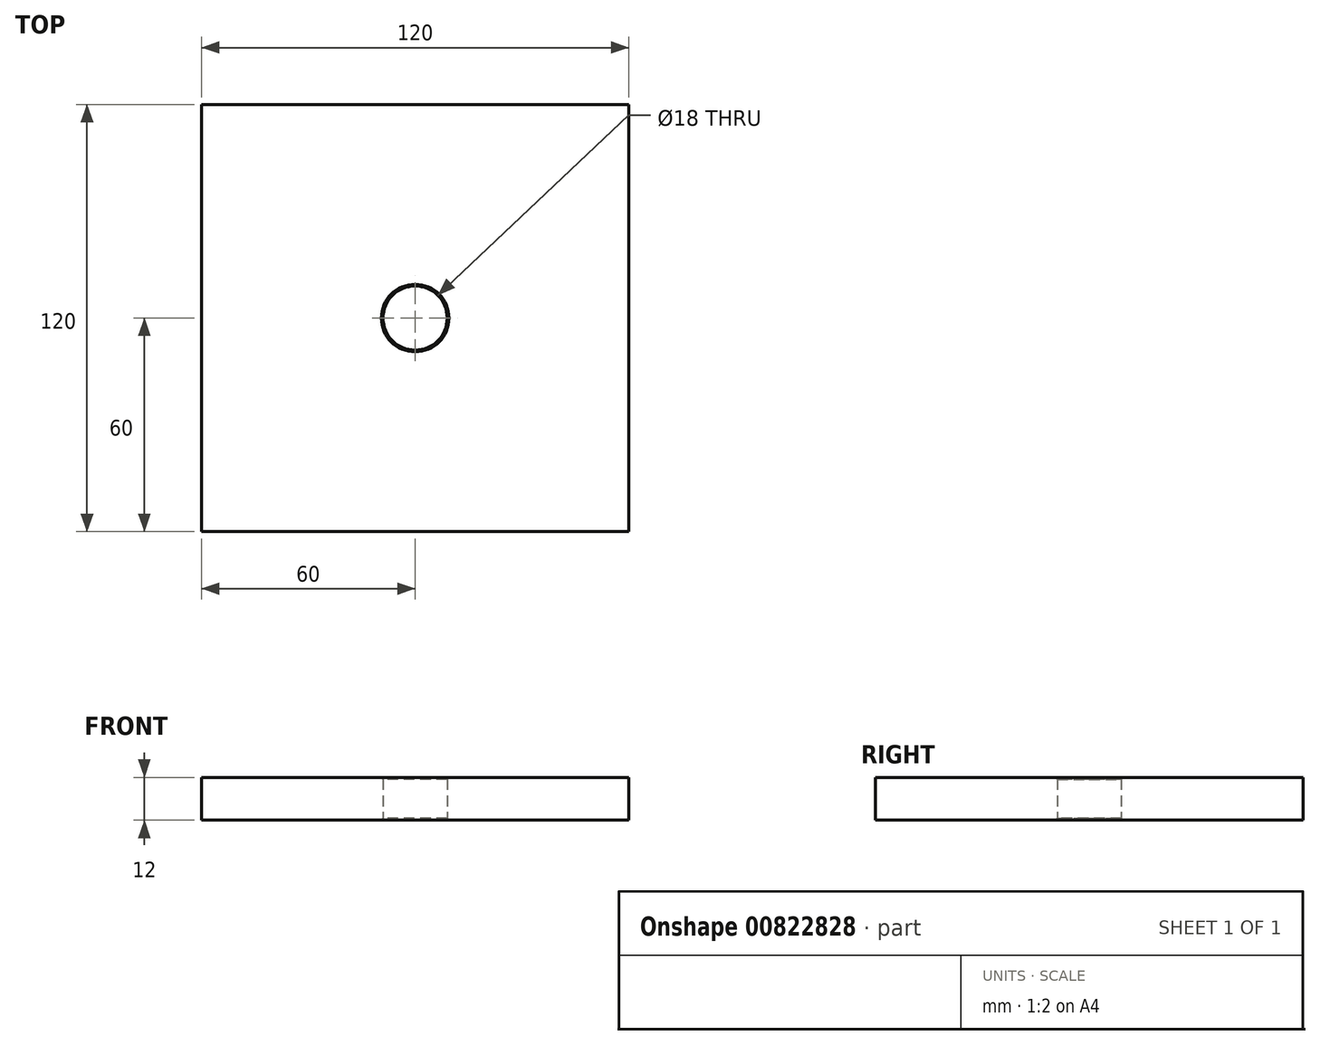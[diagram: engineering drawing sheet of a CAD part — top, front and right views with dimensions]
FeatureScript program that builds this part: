
annotation { "Feature Type Name" : "Feature", "Feature Type Description" : "" }
export const myFeature = defineFeature(function(context is Context, id is Id, definition is map)
    precondition{}
    {
        {
            var Q0;
            Q0=qCreatedBy(makeId("Top.planeOp"),FACE);
            var sketch = newSketch(context, id + "F0", { "sketchPlane" : qUnion([Q0])});
            skLineSegment(sketch, "E0.bottom", {"start": v(-60, -60) * mm, "end": v(60, -60) * mm});
            skLineSegment(sketch, "E0.top", {"start": v(-60, 60) * mm, "end": v(60, 60) * mm});
            skLineSegment(sketch, "E0.left", {"start": v(-60, -60) * mm, "end": v(-60, 60) * mm});
            skLineSegment(sketch, "E0.right", {"start": v(60, -60) * mm, "end": v(60, 60) * mm});
            skPoint(sketch, "E0.middle", {"position": v(0, 0) * mm});
            skLineSegment(sketch, "E1", {"start": v(0, 0) * mm, "end": v(0, 29.5) * mm, "construction": true});
            skLineSegment(sketch, "E2.bottom", {"start": v(-50.7, 9) * mm, "end": v(50.7, 9) * mm, "construction": true});
            skLineSegment(sketch, "E2.top", {"start": v(-50.7, 50) * mm, "end": v(50.7, 50) * mm, "construction": true});
            skLineSegment(sketch, "E2.left", {"start": v(-50.7, 9) * mm, "end": v(-50.7, 50) * mm, "construction": true});
            skLineSegment(sketch, "E2.right", {"start": v(50.7, 9) * mm, "end": v(50.7, 50) * mm, "construction": true});
            skPoint(sketch, "E2.middle", {"position": v(0, 29.5) * mm});
            skLineSegment(sketch, "E3.0", {"start": v(-50.7, 43.7) * mm, "end": v(50.7, 43.7) * mm, "construction": true});
            skCircle(sketch, "E4", {"center": v(0, 0) * mm, "radius": 9 * mm});
            skSolve(sketch);
        }
        {
            var Q0;
            Q0 = qSketchRegion(id + "F0", true);
            extrude(context, id + "F1", {"entities" : qUnion([Q0]), "depth" : 12 * mm, "offsetDistance" : 25 * mm});
        }
        {
            var Q0;
            Q0=makeQuery(id+"F1.opExtrude","SWEPT_FACE",FACE,{"disambiguationData":[OSD([sQuery(id+"F0.wireOp",EDGE,"E4")])]});
            chamfer(context, id + "F2", {"entities" : qUnion([Q0]), "width" : 0.5 * mm, "tangentPropagation" : true});
        }
    });
